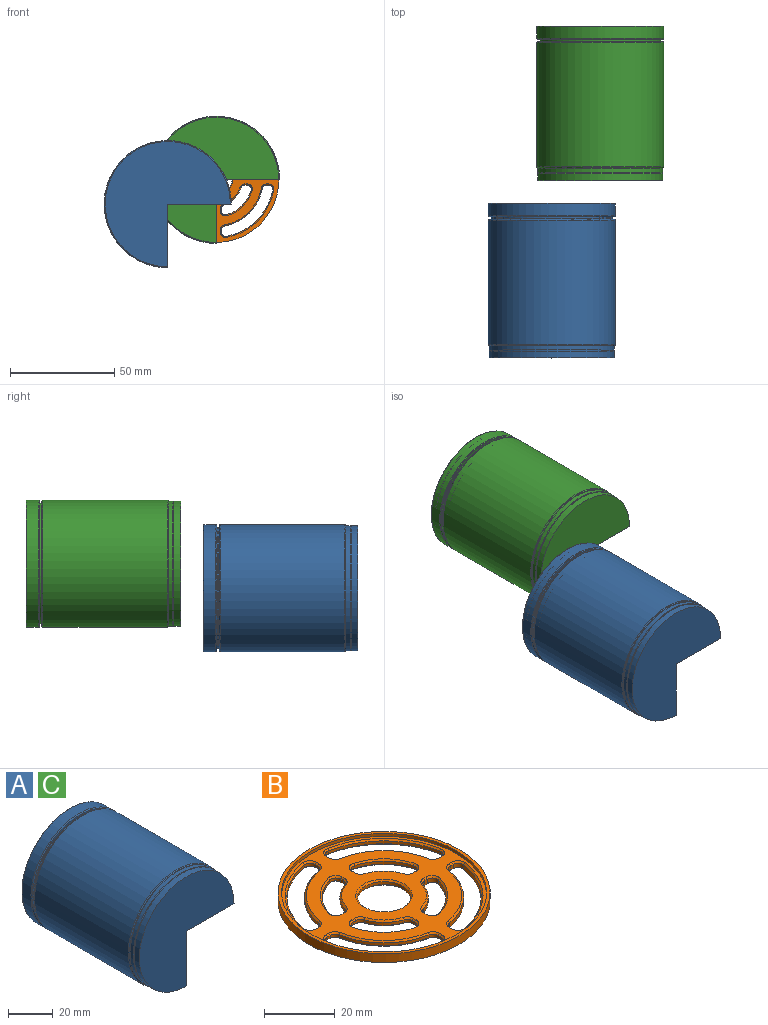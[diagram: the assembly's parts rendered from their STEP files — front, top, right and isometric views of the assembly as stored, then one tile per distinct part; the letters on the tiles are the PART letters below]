
ASSEMBLY  parts=3 mates=1
PART A: 32 faces, bbox 66x74x66 mm
  f0: plane 58.55x58.55mm, normal (0,1,0), area 2019.5mm2, adj f19,f20,f21
  f1: plane 60x60mm, normal (0,-1,0), area 2120.6mm2, adj f2,f20,f21
  f2: cylinder r=30mm len=60mm, axis (0,1,0), area 459.5mm2, adj f1,f3,f20,f21
  f3: torus R=30mm, axis (0,1,0), area 110.4mm2, adj f2,f4,f20,f21
  f4: cylinder r=30mm len=60mm, axis (0,1,0), area 289.8mm2, adj f3,f20,f21,f23
  f5: cylinder r=30.5mm len=61mm, axis (0,1,0), area 8544.1mm2, adj f20,f21,f29,f31
  f6: plane 60x60mm, normal (0,1,0), area 111.6mm2, adj f20,f21,f24,f29
  f7: cylinder r=29mm len=58mm, axis (0,1,0), area 120.6mm2, adj f20,f21,f24,f25
  f8: plane 60x60mm, normal (0,-1,0), area 111.6mm2, adj f20,f21,f25,f30
  f9: cylinder r=30.5mm len=61mm, axis (0,1,0), area 804.9mm2, adj f20,f21,f26,f30
  f10: plane 60.6x60.6mm, normal (0,1,0), area 14.3mm2, adj f20,f21,f26,f27
  f11: cylinder r=30mm len=60mm, axis (0,1,0), area 289.8mm2, adj f12,f20,f21,f27
  f12: torus R=30mm, axis (0,1,0), area 110.4mm2, adj f11,f13,f20,f21
  f13: cylinder r=30mm len=60mm, axis (0,1,0), area 459.5mm2, adj f12,f14,f20,f21
  f14: plane 60x60mm, normal (0,1,0), area 166.3mm2, adj f13,f15,f20,f21
  f15: torus R=28.8mm, axis (0,1,0), area 167.5mm2, adj f14,f16,f20,f21
  f16: cylinder r=28mm len=56mm, axis (0,1,0), area 37.3mm2, adj f15,f17,f20,f21
  f17: torus R=28.8mm, axis (0,1,0), area 114.3mm2, adj f16,f20,f21,f22
  f18: cylinder r=30mm len=60mm, axis (0,1,0), area 8096.5mm2, adj f20,f21,f22,f28
  f19: cylinder r=29.28mm len=58.55mm, axis (0,1,0), area 445.4mm2, adj f0,f20,f21,f28
  f20: plane 74x30.5mm, normal (1,0,0), area 73.3mm2, adj f0,f1,f2,f3,f4,f5,f6,f7
  f21: plane 74x30.5mm, normal (0,0,-1), area 73.3mm2, adj f0,f1,f2,f3,f4,f5,f6,f7
  f22: torus R=27mm, axis (0,1,0), area 448.6mm2, adj f17,f18,f20,f21
  f23: torus R=30.2mm, axis (0,-1,0), area 36.3mm2, adj f4,f20,f21,f31
  f24: torus R=29.2mm, axis (0,1,0), area 43mm2, adj f6,f7,f20,f21
  f25: torus R=29.2mm, axis (0,1,0), area 43mm2, adj f7,f8,f20,f21
  f26: torus R=30.3mm, axis (0,1,0), area 45mm2, adj f9,f10,f20,f21
  f27: torus R=30.2mm, axis (0,1,0), area 44.5mm2, adj f10,f11,f20,f21
  f28: torus R=32.28mm, axis (0,1,0), area 296.1mm2, adj f18,f19,f20,f21
  f29: torus R=30mm, axis (0,1,0), area 112.2mm2, adj f5,f6,f20,f21
  f30: torus R=30mm, axis (0,1,0), area 112.2mm2, adj f8,f9,f20,f21
  f31: torus R=30mm, axis (0,-1,0), area 91.7mm2, adj f5,f20,f21,f23
PART B: 184 faces, bbox 60x60x3 mm
  f0: plane 58x58mm, normal (0,0,1), area 1171.2mm2, adj f76,f77,f78,f79,f80,f81,f82,f83
  f1: plane 60x60mm, normal (0,0,-1), area 1417.4mm2, adj f2,f3,f4,f5,f6,f16,f17,f18
  f2: cylinder r=30mm len=60mm, axis (0,0,-1), area 565.5mm2, adj f1,f183
  f3: plane 1.5x1.02mm, normal (1,0,0), area 1.5mm2, adj f1,f64,f67,f168
  f4: cylinder r=27.5mm len=22.22mm, axis (0,0,-1), area 50.2mm2, adj f1,f66,f67,f171
  f5: plane 1.5x1.02mm, normal (0,-1,0), area 1.5mm2, adj f1,f65,f66,f167
  f6: cylinder r=22.5mm len=17.98mm, axis (0,0,-1), area 40.5mm2, adj f1,f64,f65,f164
  f7: cylinder r=12.5mm len=8mm, axis (0,0,-1), area 11.7mm2, adj f44,f47,f101,f130
  f8: plane 1.05x1mm, normal (-1,0,0), area 1mm2, adj f46,f47,f105,f129
  f9: cylinder r=17.5mm len=11.67mm, axis (0,0,-1), area 17.2mm2, adj f45,f46,f106,f125
  f10: plane 1.05x1mm, normal (0,1,0), area 1mm2, adj f44,f45,f102,f126
  f11: cylinder r=12.5mm len=8mm, axis (0,0,-1), area 11.7mm2, adj f40,f43,f155,f163
  f12: plane 1.05x1mm, normal (0,-1,0), area 1mm2, adj f42,f43,f151,f160
  f13: cylinder r=17.5mm len=11.67mm, axis (0,0,-1), area 17.2mm2, adj f41,f42,f148,f156
  f14: plane 1.05x1mm, normal (-1,0,0), area 1mm2, adj f40,f41,f152,f159
  f15: cylinder r=7.5mm len=15mm, axis (0,0,-1), area 47.1mm2, adj f180,f181
  f16: plane 1.5x1.05mm, normal (1,0,0), area 1.6mm2, adj f1,f36,f39,f176
  f17: cylinder r=17.5mm len=11.67mm, axis (0,0,-1), area 25.8mm2, adj f1,f38,f39,f179
  f18: plane 1.5x1.05mm, normal (0,-1,0), area 1.6mm2, adj f1,f37,f38,f175
  f19: cylinder r=12.5mm len=8mm, axis (0,0,-1), area 17.6mm2, adj f1,f36,f37,f172
  f20: plane 1.02x1mm, normal (1,0,0), area 1mm2, adj f60,f63,f72,f79
  f21: cylinder r=22.5mm len=17.98mm, axis (0,0,-1), area 27mm2, adj f60,f61,f68,f76
  f22: plane 1.02x1mm, normal (0,1,0), area 1mm2, adj f61,f62,f71,f80
  f23: cylinder r=27.5mm len=22.22mm, axis (0,0,-1), area 33.4mm2, adj f62,f63,f75,f83
  f24: cylinder r=27.5mm len=22.22mm, axis (0,0,-1), area 33.4mm2, adj f56,f59,f134,f141
  f25: plane 1.02x1mm, normal (-1,0,0), area 1mm2, adj f58,f59,f133,f142
  f26: cylinder r=22.5mm len=17.98mm, axis (0,0,-1), area 27mm2, adj f57,f58,f137,f146
  f27: plane 1.02x1mm, normal (0,-1,0), area 1mm2, adj f56,f57,f138,f145
  f28: cylinder r=22.5mm len=17.98mm, axis (0,0,-1), area 27mm2, adj f52,f55,f109,f118
  f29: plane 1.02x1mm, normal (-1,0,0), area 1mm2, adj f54,f55,f113,f122
  f30: cylinder r=27.5mm len=22.22mm, axis (0,0,-1), area 33.4mm2, adj f53,f54,f114,f121
  f31: plane 1.02x1mm, normal (0,1,0), area 1mm2, adj f52,f53,f110,f117
  f32: plane 1.05x1mm, normal (1,0,0), area 1mm2, adj f48,f51,f88,f95
  f33: cylinder r=12.5mm len=8mm, axis (0,0,-1), area 11.7mm2, adj f50,f51,f84,f92
  f34: plane 1.05x1mm, normal (0,1,0), area 1mm2, adj f49,f50,f87,f96
  f35: cylinder r=17.5mm len=11.67mm, axis (0,0,-1), area 17.2mm2, adj f48,f49,f91,f99
  f36: cylinder r=2mm len=1.9mm, axis (0,0,-1), area 3.8mm2, adj f1,f16,f19,f174
  f37: cylinder r=2mm len=1.9mm, axis (0,0,-1), area 3.8mm2, adj f1,f18,f19,f173
  f38: cylinder r=2mm len=2.58mm, axis (0,0,-1), area 5.6mm2, adj f1,f17,f18,f177
  f39: cylinder r=2mm len=2.58mm, axis (0,0,-1), area 5.6mm2, adj f1,f16,f17,f178
  f40: cylinder r=2mm len=1.9mm, axis (0,0,-1), area 2.5mm2, adj f11,f14,f154,f161
  f41: cylinder r=2mm len=2.58mm, axis (0,0,-1), area 3.7mm2, adj f13,f14,f150,f157
  f42: cylinder r=2mm len=2.58mm, axis (0,0,-1), area 3.7mm2, adj f12,f13,f149,f158
  f43: cylinder r=2mm len=1.9mm, axis (0,0,-1), area 2.5mm2, adj f11,f12,f153,f162
  f44: cylinder r=2mm len=1.9mm, axis (0,0,-1), area 2.5mm2, adj f7,f10,f100,f128
  f45: cylinder r=2mm len=2.58mm, axis (0,0,-1), area 3.7mm2, adj f9,f10,f104,f124
  f46: cylinder r=2mm len=2.58mm, axis (0,0,-1), area 3.7mm2, adj f8,f9,f107,f127
  f47: cylinder r=2mm len=1.9mm, axis (0,0,-1), area 2.5mm2, adj f7,f8,f103,f131
  f48: cylinder r=2mm len=2.58mm, axis (0,0,-1), area 3.7mm2, adj f32,f35,f90,f97
  f49: cylinder r=2mm len=2.58mm, axis (0,0,-1), area 3.7mm2, adj f34,f35,f89,f98
  f50: cylinder r=2mm len=1.9mm, axis (0,0,-1), area 2.5mm2, adj f33,f34,f85,f94
  f51: cylinder r=2mm len=1.9mm, axis (0,0,-1), area 2.5mm2, adj f32,f33,f86,f93
  f52: cylinder r=2mm len=1.97mm, axis (0,0,-1), area 2.8mm2, adj f28,f31,f108,f116
  f53: cylinder r=2mm len=2.35mm, axis (0,0,-1), area 3.5mm2, adj f30,f31,f112,f119
  f54: cylinder r=2mm len=2.35mm, axis (0,0,-1), area 3.5mm2, adj f29,f30,f115,f123
  f55: cylinder r=2mm len=1.97mm, axis (0,0,-1), area 2.8mm2, adj f28,f29,f111,f120
  f56: cylinder r=2mm len=2.35mm, axis (0,0,-1), area 3.5mm2, adj f24,f27,f136,f143
  f57: cylinder r=2mm len=1.97mm, axis (0,0,-1), area 2.8mm2, adj f26,f27,f139,f147
  f58: cylinder r=2mm len=1.97mm, axis (0,0,-1), area 2.8mm2, adj f25,f26,f135,f144
  f59: cylinder r=2mm len=2.35mm, axis (0,0,-1), area 3.5mm2, adj f24,f25,f132,f140
  f60: cylinder r=2mm len=1.97mm, axis (0,0,-1), area 2.8mm2, adj f20,f21,f70,f77
  f61: cylinder r=2mm len=1.97mm, axis (0,0,-1), area 2.8mm2, adj f21,f22,f69,f78
  f62: cylinder r=2mm len=2.35mm, axis (0,0,-1), area 3.5mm2, adj f22,f23,f73,f82
  f63: cylinder r=2mm len=2.35mm, axis (0,0,-1), area 3.5mm2, adj f20,f23,f74,f81
  f64: cylinder r=2mm len=1.97mm, axis (0,0,-1), area 4.2mm2, adj f1,f3,f6,f166
  f65: cylinder r=2mm len=1.97mm, axis (0,0,-1), area 4.2mm2, adj f1,f5,f6,f165
  f66: cylinder r=2mm len=2.35mm, axis (0,0,-1), area 5.2mm2, adj f1,f4,f5,f169
  f67: cylinder r=2mm len=2.35mm, axis (0,0,-1), area 5.2mm2, adj f1,f3,f4,f170
  f68: cone r=22.5mm half-angle=45deg, axis (0,0,1), area 18.9mm2, adj f1,f21,f69,f70
  f69: cone r=2.5mm half-angle=45deg, axis (0,0,-1), area 2.2mm2, adj f1,f61,f68,f71
  f70: cone r=2.5mm half-angle=45deg, axis (0,0,-1), area 2.2mm2, adj f1,f60,f68,f72
  f71: plane 1.02x0.5mm, normal (0,0.71,-0.71), area 0.7mm2, adj f1,f22,f69,f73
  f72: plane 1.02x0.5mm, normal (0.71,0,-0.71), area 0.7mm2, adj f1,f20,f70,f74
  f73: cone r=2.5mm half-angle=45deg, axis (0,0,-1), area 2.8mm2, adj f1,f62,f71,f75
  f74: cone r=2.5mm half-angle=45deg, axis (0,0,-1), area 2.8mm2, adj f1,f63,f72,f75
  f75: cone r=28mm half-angle=45deg, axis (0,0,-1), area 23.9mm2, adj f1,f23,f73,f74
  f76: cone r=22.5mm half-angle=45deg, axis (0,0,-1), area 18.9mm2, adj f0,f21,f77,f78
  f77: cone r=2.5mm half-angle=45deg, axis (0,0,1), area 2.2mm2, adj f0,f60,f76,f79
  f78: cone r=2.5mm half-angle=45deg, axis (0,0,1), area 2.2mm2, adj f0,f61,f76,f80
  f79: plane 1.02x0.5mm, normal (0.71,0,0.71), area 0.7mm2, adj f0,f20,f77,f81
  f80: plane 1.02x0.5mm, normal (0,0.71,0.71), area 0.7mm2, adj f0,f22,f78,f82
  f81: cone r=2.5mm half-angle=45deg, axis (0,0,1), area 2.8mm2, adj f0,f63,f79,f83
  f82: cone r=2.5mm half-angle=45deg, axis (0,0,1), area 2.8mm2, adj f0,f62,f80,f83
  f83: cone r=28mm half-angle=45deg, axis (0,0,1), area 23.9mm2, adj f0,f23,f81,f82
  f84: cone r=12.5mm half-angle=45deg, axis (0,0,1), area 8.1mm2, adj f1,f33,f85,f86
  f85: cone r=2.5mm half-angle=45deg, axis (0,0,-1), area 2mm2, adj f1,f50,f84,f87
  f86: cone r=2.5mm half-angle=45deg, axis (0,0,-1), area 2mm2, adj f1,f51,f84,f88
  f87: plane 1.05x0.5mm, normal (0,0.71,-0.71), area 0.7mm2, adj f1,f34,f85,f89
  f88: plane 1.05x0.5mm, normal (0.71,0,-0.71), area 0.7mm2, adj f1,f32,f86,f90
  f89: cone r=2.5mm half-angle=45deg, axis (0,0,-1), area 3mm2, adj f1,f49,f87,f91
  f90: cone r=2.5mm half-angle=45deg, axis (0,0,-1), area 3mm2, adj f1,f48,f88,f91
  f91: cone r=18mm half-angle=45deg, axis (0,0,-1), area 12.3mm2, adj f1,f35,f89,f90
  f92: cone r=12.5mm half-angle=45deg, axis (0,0,-1), area 8.1mm2, adj f0,f33,f93,f94
  f93: cone r=2.5mm half-angle=45deg, axis (0,0,1), area 2mm2, adj f0,f51,f92,f95
  f94: cone r=2.5mm half-angle=45deg, axis (0,0,1), area 2mm2, adj f0,f50,f92,f96
  f95: plane 1.05x0.5mm, normal (0.71,0,0.71), area 0.7mm2, adj f0,f32,f93,f97
  f96: plane 1.05x0.5mm, normal (0,0.71,0.71), area 0.7mm2, adj f0,f34,f94,f98
  f97: cone r=2.5mm half-angle=45deg, axis (0,0,1), area 3mm2, adj f0,f48,f95,f99
  f98: cone r=2.5mm half-angle=45deg, axis (0,0,1), area 3mm2, adj f0,f49,f96,f99
  f99: cone r=18mm half-angle=45deg, axis (0,0,1), area 12.3mm2, adj f0,f35,f97,f98
  f100: cone r=2.5mm half-angle=45deg, axis (0,0,-1), area 2mm2, adj f1,f44,f101,f102
  f101: cone r=12.5mm half-angle=45deg, axis (0,0,1), area 8.1mm2, adj f1,f7,f100,f103
  f102: plane 1.05x0.5mm, normal (0,0.71,-0.71), area 0.7mm2, adj f1,f10,f100,f104
  f103: cone r=2.5mm half-angle=45deg, axis (0,0,-1), area 2mm2, adj f1,f47,f101,f105
  f104: cone r=2.5mm half-angle=45deg, axis (0,0,-1), area 3mm2, adj f1,f45,f102,f106
  f105: plane 1.05x0.5mm, normal (-0.71,0,-0.71), area 0.7mm2, adj f1,f8,f103,f107
  f106: cone r=18mm half-angle=45deg, axis (0,0,-1), area 12.3mm2, adj f1,f9,f104,f107
  f107: cone r=2.5mm half-angle=45deg, axis (0,0,-1), area 3mm2, adj f1,f46,f105,f106
  f108: cone r=2.5mm half-angle=45deg, axis (0,0,-1), area 2.2mm2, adj f1,f52,f109,f110
  f109: cone r=22.5mm half-angle=45deg, axis (0,0,1), area 18.9mm2, adj f1,f28,f108,f111
  f110: plane 1.02x0.5mm, normal (0,0.71,-0.71), area 0.7mm2, adj f1,f31,f108,f112
  f111: cone r=2.5mm half-angle=45deg, axis (0,0,-1), area 2.2mm2, adj f1,f55,f109,f113
  f112: cone r=2.5mm half-angle=45deg, axis (0,0,-1), area 2.8mm2, adj f1,f53,f110,f114
  f113: plane 1.02x0.5mm, normal (-0.71,0,-0.71), area 0.7mm2, adj f1,f29,f111,f115
  f114: cone r=28mm half-angle=45deg, axis (0,0,-1), area 23.9mm2, adj f1,f30,f112,f115
  f115: cone r=2.5mm half-angle=45deg, axis (0,0,-1), area 2.8mm2, adj f1,f54,f113,f114
  f116: cone r=2.5mm half-angle=45deg, axis (0,0,1), area 2.2mm2, adj f0,f52,f117,f118
  f117: plane 1.02x0.5mm, normal (0,0.71,0.71), area 0.7mm2, adj f0,f31,f116,f119
  f118: cone r=22.5mm half-angle=45deg, axis (0,0,-1), area 18.9mm2, adj f0,f28,f116,f120
  f119: cone r=2.5mm half-angle=45deg, axis (0,0,1), area 2.8mm2, adj f0,f53,f117,f121
  f120: cone r=2.5mm half-angle=45deg, axis (0,0,1), area 2.2mm2, adj f0,f55,f118,f122
  f121: cone r=28mm half-angle=45deg, axis (0,0,1), area 23.9mm2, adj f0,f30,f119,f123
  f122: plane 1.02x0.5mm, normal (-0.71,0,0.71), area 0.7mm2, adj f0,f29,f120,f123
  f123: cone r=2.5mm half-angle=45deg, axis (0,0,1), area 2.8mm2, adj f0,f54,f121,f122
  f124: cone r=2.5mm half-angle=45deg, axis (0,0,1), area 3mm2, adj f0,f45,f125,f126
  f125: cone r=18mm half-angle=45deg, axis (0,0,1), area 12.3mm2, adj f0,f9,f124,f127
  f126: plane 1.05x0.5mm, normal (0,0.71,0.71), area 0.7mm2, adj f0,f10,f124,f128
  f127: cone r=2.5mm half-angle=45deg, axis (0,0,1), area 3mm2, adj f0,f46,f125,f129
  f128: cone r=2.5mm half-angle=45deg, axis (0,0,1), area 2mm2, adj f0,f44,f126,f130
  f129: plane 1.05x0.5mm, normal (-0.71,0,0.71), area 0.7mm2, adj f0,f8,f127,f131
  f130: cone r=12.5mm half-angle=45deg, axis (0,0,-1), area 8.1mm2, adj f0,f7,f128,f131
  f131: cone r=2.5mm half-angle=45deg, axis (0,0,1), area 2mm2, adj f0,f47,f129,f130
  f132: cone r=2.5mm half-angle=45deg, axis (0,0,-1), area 2.8mm2, adj f1,f59,f133,f134
  f133: plane 1.02x0.5mm, normal (-0.71,0,-0.71), area 0.7mm2, adj f1,f25,f132,f135
  f134: cone r=28mm half-angle=45deg, axis (0,0,-1), area 23.9mm2, adj f1,f24,f132,f136
  f135: cone r=2.5mm half-angle=45deg, axis (0,0,-1), area 2.2mm2, adj f1,f58,f133,f137
  f136: cone r=2.5mm half-angle=45deg, axis (0,0,-1), area 2.8mm2, adj f1,f56,f134,f138
  f137: cone r=22.5mm half-angle=45deg, axis (0,0,1), area 18.9mm2, adj f1,f26,f135,f139
  f138: plane 1.02x0.5mm, normal (0,-0.71,-0.71), area 0.7mm2, adj f1,f27,f136,f139
  f139: cone r=2.5mm half-angle=45deg, axis (0,0,-1), area 2.2mm2, adj f1,f57,f137,f138
  f140: cone r=2.5mm half-angle=45deg, axis (0,0,1), area 2.8mm2, adj f0,f59,f141,f142
  f141: cone r=28mm half-angle=45deg, axis (0,0,1), area 23.9mm2, adj f0,f24,f140,f143
  f142: plane 1.02x0.5mm, normal (-0.71,0,0.71), area 0.7mm2, adj f0,f25,f140,f144
  f143: cone r=2.5mm half-angle=45deg, axis (0,0,1), area 2.8mm2, adj f0,f56,f141,f145
  f144: cone r=2.5mm half-angle=45deg, axis (0,0,1), area 2.2mm2, adj f0,f58,f142,f146
  f145: plane 1.02x0.5mm, normal (0,-0.71,0.71), area 0.7mm2, adj f0,f27,f143,f147
  f146: cone r=22.5mm half-angle=45deg, axis (0,0,-1), area 18.9mm2, adj f0,f26,f144,f147
  f147: cone r=2.5mm half-angle=45deg, axis (0,0,1), area 2.2mm2, adj f0,f57,f145,f146
  f148: cone r=18mm half-angle=45deg, axis (0,0,-1), area 12.3mm2, adj f1,f13,f149,f150
  f149: cone r=2.5mm half-angle=45deg, axis (0,0,-1), area 3mm2, adj f1,f42,f148,f151
  f150: cone r=2.5mm half-angle=45deg, axis (0,0,-1), area 3mm2, adj f1,f41,f148,f152
  f151: plane 1.05x0.5mm, normal (0,-0.71,-0.71), area 0.7mm2, adj f1,f12,f149,f153
  f152: plane 1.05x0.5mm, normal (-0.71,0,-0.71), area 0.7mm2, adj f1,f14,f150,f154
  f153: cone r=2.5mm half-angle=45deg, axis (0,0,-1), area 2mm2, adj f1,f43,f151,f155
  f154: cone r=2.5mm half-angle=45deg, axis (0,0,-1), area 2mm2, adj f1,f40,f152,f155
  f155: cone r=12.5mm half-angle=45deg, axis (0,0,1), area 8.1mm2, adj f1,f11,f153,f154
  f156: cone r=18mm half-angle=45deg, axis (0,0,1), area 12.3mm2, adj f0,f13,f157,f158
  f157: cone r=2.5mm half-angle=45deg, axis (0,0,1), area 3mm2, adj f0,f41,f156,f159
  f158: cone r=2.5mm half-angle=45deg, axis (0,0,1), area 3mm2, adj f0,f42,f156,f160
  f159: plane 1.05x0.5mm, normal (-0.71,0,0.71), area 0.7mm2, adj f0,f14,f157,f161
  f160: plane 1.05x0.5mm, normal (0,-0.71,0.71), area 0.7mm2, adj f0,f12,f158,f162
  f161: cone r=2.5mm half-angle=45deg, axis (0,0,1), area 2mm2, adj f0,f40,f159,f163
  f162: cone r=2.5mm half-angle=45deg, axis (0,0,1), area 2mm2, adj f0,f43,f160,f163
  f163: cone r=12.5mm half-angle=45deg, axis (0,0,-1), area 8.1mm2, adj f0,f11,f161,f162
  f164: cone r=22.5mm half-angle=45deg, axis (0,0,-1), area 18.9mm2, adj f0,f6,f165,f166
  f165: cone r=2.5mm half-angle=45deg, axis (0,0,1), area 2.2mm2, adj f0,f65,f164,f167
  f166: cone r=2.5mm half-angle=45deg, axis (0,0,1), area 2.2mm2, adj f0,f64,f164,f168
  f167: plane 1.02x0.5mm, normal (0,-0.71,0.71), area 0.7mm2, adj f0,f5,f165,f169
  f168: plane 1.02x0.5mm, normal (0.71,0,0.71), area 0.7mm2, adj f0,f3,f166,f170
  f169: cone r=2.5mm half-angle=45deg, axis (0,0,1), area 2.8mm2, adj f0,f66,f167,f171
  f170: cone r=2.5mm half-angle=45deg, axis (0,0,1), area 2.8mm2, adj f0,f67,f168,f171
  f171: cone r=28mm half-angle=45deg, axis (0,0,1), area 23.9mm2, adj f0,f4,f169,f170
  f172: cone r=12.5mm half-angle=45deg, axis (0,0,-1), area 8.1mm2, adj f0,f19,f173,f174
  f173: cone r=2.5mm half-angle=45deg, axis (0,0,1), area 2mm2, adj f0,f37,f172,f175
  f174: cone r=2.5mm half-angle=45deg, axis (0,0,1), area 2mm2, adj f0,f36,f172,f176
  f175: plane 1.05x0.5mm, normal (0,-0.71,0.71), area 0.7mm2, adj f0,f18,f173,f177
  f176: plane 1.05x0.5mm, normal (0.71,0,0.71), area 0.7mm2, adj f0,f16,f174,f178
  f177: cone r=2.5mm half-angle=45deg, axis (0,0,1), area 3mm2, adj f0,f38,f175,f179
  f178: cone r=2.5mm half-angle=45deg, axis (0,0,1), area 3mm2, adj f0,f39,f176,f179
  f179: cone r=18mm half-angle=45deg, axis (0,0,1), area 12.3mm2, adj f0,f17,f177,f178
  f180: cone r=8mm half-angle=45deg, axis (0,0,-1), area 34.4mm2, adj f1,f15
  f181: cone r=8mm half-angle=45deg, axis (0,0,1), area 34.4mm2, adj f0,f15
  f182: cylinder r=29mm len=58mm, axis (0,0,-1), area 182.2mm2, adj f0,f183
  f183: plane 60x60mm, normal (0,0,1), area 185.4mm2, adj f2,f182
PART C: same geometry as A
PLACE A t=(-9.06,-0.59,-18.97)mm
PLACE B rot(axis=(-1,0,0),90deg) t=(14.16,84.42,-7.32)mm
PLACE C t=(14.16,84.42,-7.32)mm
MATE fastened B.f17 <-> C.f2  axis (0,-1,0) through (14.16,84.42,-7.32)mm
